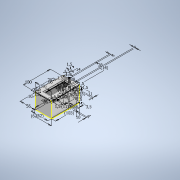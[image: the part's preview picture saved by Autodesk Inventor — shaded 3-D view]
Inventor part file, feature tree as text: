
AUTODESK INVENTOR PART (.ipt)
format: ipt  version: 2020 (Build 240168000, 168)  size: 405,504 bytes
history: native  units: mm
features: extrude x21, sketch x7
ambient origin geometry x8: Origin, YZ Plane, XZ Plane, XY Plane, X Axis, Y Axis, Z Axis, Center Point
bodies: Volumenkörper1 (feature_tree)
feature tree (28):
  sketch  "Skizze1"  dims[d0=100.0mm d1=56.0mm]
  extrude  "Extrusion1"  Depth=56.0mm
  extrude  "Extrusion2"  Depth=1.5mm
  extrude  "Extrusion3"  Depth=1.5mm
  extrude  "Extrusion4"  Depth=78.0mm
  sketch  "Skizze3"  dims[d4=1.5mm d5=1.5mm]
  extrude  "Extrusion5"  Depth=11.0mm
  extrude  "Extrusion6"  Depth=4.0mm
  extrude  "Extrusion7"  Depth=4.0mm
  extrude  "Extrusion8"  Depth=14.0mm
  extrude  "Extrusion9"  Depth=14.0mm
  extrude  "Extrusion10"  Depth=3.0mm TaperAngle=0.0deg
  extrude  "Extrusion11"  Depth=3.0mm TaperAngle=0.0deg
  sketch  "Skizze6"  dims[d8=11.0mm d9=11.0mm]
  extrude  "Extrusion12"  Depth=1.5mm TaperAngle=0.0deg
  extrude  "Extrusion13"  Depth=2.0mm TaperAngle=0.0deg
  extrude  "Extrusion14"  Depth=82.0mm
  sketch  "Skizze7"  dims[d10=4.0mm d11=4.0mm]
  sketch  "Skizze8"  dims[d12=4.0mm d13=4.0mm d14=14.0mm d15=14.0mm d16=3.0mm d17=55.0mm d18=0.0mm d19=0.0mm d20=3.0mm d21=0.0mm d22=1.5mm d23=0.0mm d24=2.0mm d25=0.0mm d26=82.0mm d27=38.0mm d28=9.0mm d29=9.0mm d30=1.5mm d31=1.5mm d32=1.5mm d33=1.5mm d39=6.0mm d40=20.0mm d41=26.0mm d42=72.0mm d43=6.0mm d44=5.0mm d45=1.0mm d46=1.5mm d47=1.5mm d48=1.5mm d49=1.5mm d50=2.5mm d51=0.0mm d52=38.0mm d53=82.0mm d54=9.0mm d55=10.0mm d56=1.5mm d57=1.5mm d58=1.5mm d59=1.5mm d60=6.0mm d61=8.0mm d62=0.0mm d63=8.0mm d64=0.0mm d65=8.0mm d66=0.0mm d67=8.0mm d68=0.0mm d69=10.0mm d70=0.0mm d71=3.0mm d72=12.0mm d73=55.0mm d74=10.0mm d75=59.0mm d76=36.0mm d77=20.0mm d78=1.5mm d79=0.0mm d80=1.5mm d81=103.0mm d82=103.0mm d83=1.5mm d84=0.0mm d85=1.5mm d86=101.5mm d87=1.5mm d88=0.0mm d90=30.0mm d91=20.0mm d92=2.5mm d93=0.0mm d94=2.5mm d95=0.0mm d96=20.0mm d97=103.0mm d98=62.0mm d99=59.0mm d100=62.0mm d101=6.5mm d102=4.0mm d103=0.0mm d104=6.5mm d105=4.0mm d106=70.0mm d107=0.0mm d108=4.0mm d109=70.0mm d110=66.0mm d111=25.0mm d112=0.0mm d113=25.0mm d114=0.0mm d115=25.0mm d116=0.0mm d117=25.0mm d118=0.0mm d119=1.5mm d120=1.5mm d121=1.5mm d122=1.5mm d123=3.0mm d124=1.5mm d125=12.0mm d126=1.5mm d127=3.5mm d128=10.0mm d129=6.5mm d130=6.5mm d131=3.25mm d132=3.25mm d133=1.5mm d134=1.5mm d135=1.5mm d136=1.5mm d137=5.0mm d138=6.5mm d139=0.0mm d140=0.0mm d141=1.5mm d142=0.0mm d143=3.5mm d144=0.0mm]
  extrude  "Extrusion15"  Depth=38.0mm
  extrude  "Extrusion16"  Depth=9.0mm
  extrude  "Extrusion17"  Depth=9.0mm
  extrude  "Extrusion18"  Depth=1.5mm
  extrude  "Extrusion19"  Depth=1.5mm
  extrude  "Extrusion20"  Depth=1.5mm
  extrude  "Extrusion21"  Depth=1.5mm
  sketch  "Skizze2"  dims[d2=1.5mm d3=1.5mm]
  sketch  "Skizze5"  dims[d6=28.0mm d7=78.0mm]
